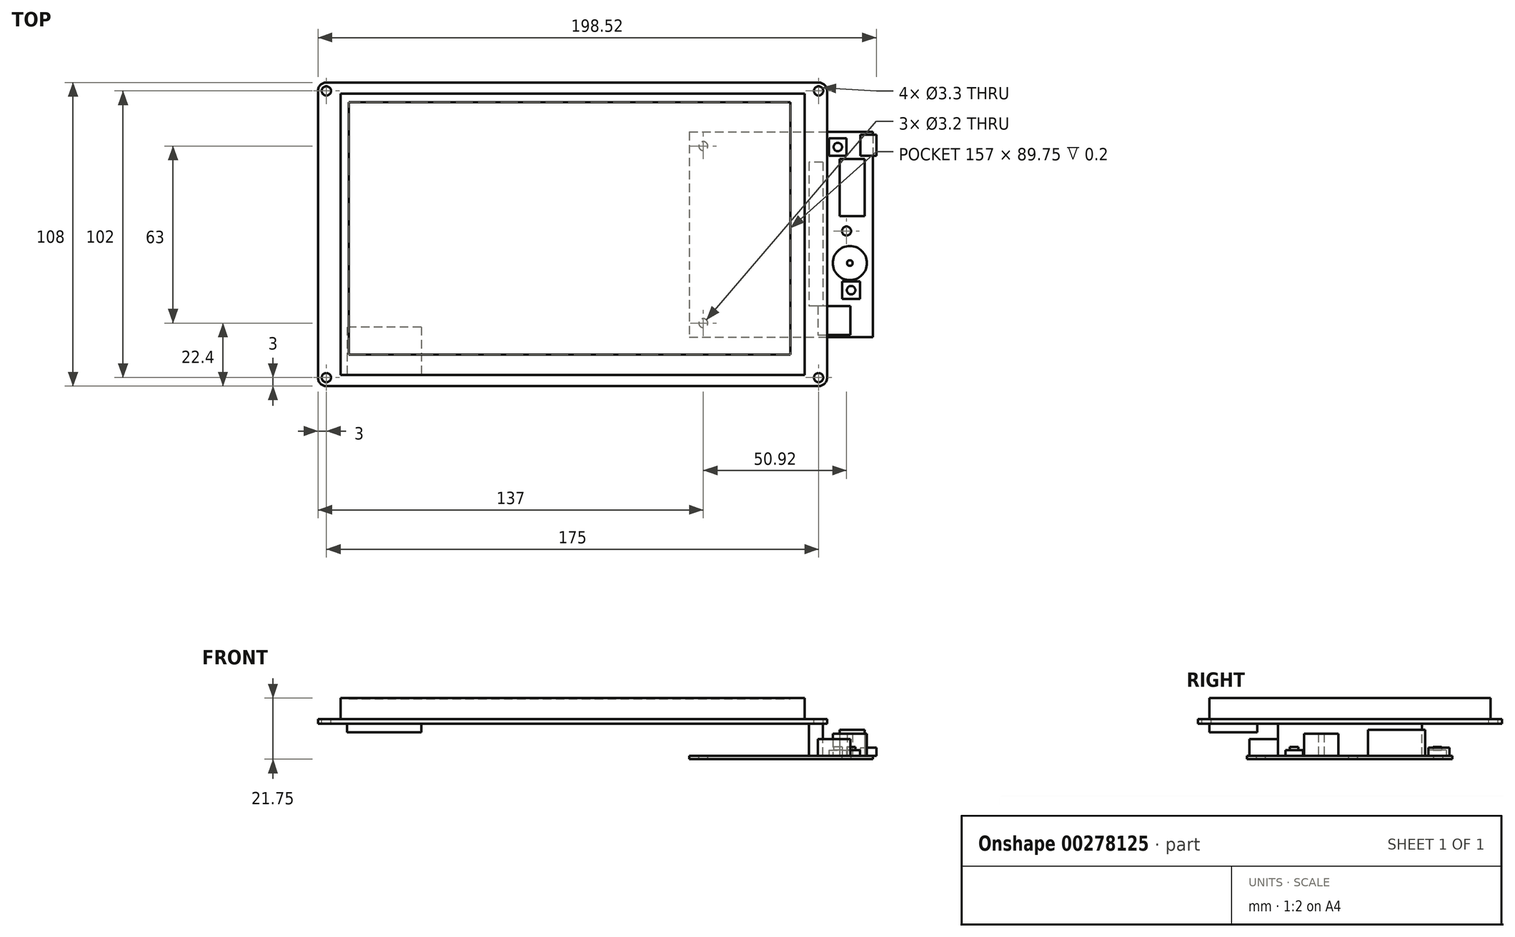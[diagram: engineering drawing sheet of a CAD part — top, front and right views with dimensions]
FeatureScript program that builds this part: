
annotation { "Feature Type Name" : "Feature", "Feature Type Description" : "" }
export const myFeature = defineFeature(function(context is Context, id is Id, definition is map)
    precondition{}
    {
        {
            var Q0;
            Q0=qCreatedBy(makeId("Top.planeOp"),FACE);
            var sketch = newSketch(context, id + "F0", { "sketchPlane" : qUnion([Q0])});
            skLineSegment(sketch, "E0.bottom", {"start": v(87.5, -54) * mm, "end": v(-87.5, -54) * mm});
            skLineSegment(sketch, "E0.top", {"start": v(87.5, 54) * mm, "end": v(-87.5, 54) * mm});
            skLineSegment(sketch, "E0.left", {"start": v(90.5, -51) * mm, "end": v(90.5, 51) * mm});
            skLineSegment(sketch, "E0.right", {"start": v(-90.5, -51) * mm, "end": v(-90.5, 51) * mm});
            skPoint(sketch, "E0.middle", {"position": v(0, 0) * mm});
            skLineSegment(sketch, "E1", {"start": v(0, 54) * mm, "end": v(0, -54) * mm, "construction": true});
            skLineSegment(sketch, "E2", {"start": v(-90.5, 0) * mm, "end": v(90.5, 0) * mm, "construction": true});
            skCircle(sketch, "E3", {"center": v(-87.5, 51) * mm, "radius": 1.65 * mm});
            skCircle(sketch, "E4.MirrorC", {"center": v(87.5, 51) * mm, "radius": 1.65 * mm});
            skCircle(sketch, "E5.MirrorC", {"center": v(-87.5, -51) * mm, "radius": 1.65 * mm});
            skCircle(sketch, "E6.MirrorC", {"center": v(87.5, -51) * mm, "radius": 1.65 * mm});
            skPoint(sketch, "E7.visualSharp", {"position": v(-90.5, 54) * mm});
            skArc(sketch, "E7.filletArc", {"start": v(-87.5, 54) * mm, "mid": v(-89.62, 53.12) * mm, "end": v(-90.5, 51) * mm});
            skPoint(sketch, "E8.visualSharp", {"position": v(-90.5, -54) * mm});
            skArc(sketch, "E8.filletArc", {"start": v(-90.5, -51) * mm, "mid": v(-89.62, -53.12) * mm, "end": v(-87.5, -54) * mm});
            skPoint(sketch, "E9.visualSharp", {"position": v(90.5, -54) * mm});
            skArc(sketch, "E9.filletArc", {"start": v(87.5, -54) * mm, "mid": v(89.62, -53.12) * mm, "end": v(90.5, -51) * mm});
            skPoint(sketch, "E10.visualSharp", {"position": v(90.5, 54) * mm});
            skArc(sketch, "E10.filletArc", {"start": v(90.5, 51) * mm, "mid": v(89.62, 53.12) * mm, "end": v(87.5, 54) * mm});
            skLineSegment(sketch, "E11.bottom", {"start": v(-82.5, 50) * mm, "end": v(82.5, 50) * mm});
            skLineSegment(sketch, "E11.top", {"start": v(-82.5, -50) * mm, "end": v(82.5, -50) * mm});
            skLineSegment(sketch, "E11.left", {"start": v(-82.5, 50) * mm, "end": v(-82.5, -50) * mm});
            skLineSegment(sketch, "E11.right", {"start": v(82.5, 50) * mm, "end": v(82.5, -50) * mm});
            skSolve(sketch);
        }
        {
            var Q0;
            Q0 = qSketchRegion(id + "F0", true);
            var Q1;
            Q1=makeQuery(id+"F0.imprint","IMPRINT",FACE,{"disambiguationData":[TD([[makeQuery(id+"F0.imprint","IMPRINT",EDGE,{"derivedFrom":sQuery(id+"F0.wireOp",EDGE,"E11.bottom")}),-1.0]])]});
            extrude(context, id + "F1", {"entities" : qUnion([Q0, Q1]), "oppositeDirection" : true, "depth" : 1.7 * mm});
        }
        {
            var Q0;
            Q0=makeQuery(id+"F0.imprint","IMPRINT",FACE,{"disambiguationData":[TD([[makeQuery(id+"F0.imprint","IMPRINT",EDGE,{"derivedFrom":sQuery(id+"F0.wireOp",EDGE,"E11.bottom")}),-1.0]])]});
            extrude(context, id + "F2", {"entities" : qUnion([Q0]), "operationType" : NewBodyOperationType.ADD, "depth" : 7.45 * mm});
        }
        {
            var Q0;
            Q0=makeQuery(id+"F2.opExtrude","CAP_FACE",FACE,{"disambiguationData":[OSD([sQuery(id+"F0.wireOp",EDGE,"E11.bottom"),sQuery(id+"F0.wireOp",EDGE,"E11.top"),sQuery(id+"F0.wireOp",EDGE,"E11.left"),sQuery(id+"F0.wireOp",EDGE,"E11.right")])],"isStart":false});
            var sketch = newSketch(context, id + "F3", { "sketchPlane" : qUnion([Q0])});
            skLineSegment(sketch, "E12.bottom", {"start": v(-79.5, 47) * mm, "end": v(77.5, 47) * mm});
            skLineSegment(sketch, "E12.top", {"start": v(-79.5, -42.75) * mm, "end": v(77.5, -42.75) * mm});
            skLineSegment(sketch, "E12.left", {"start": v(-79.5, 47) * mm, "end": v(-79.5, -42.75) * mm});
            skLineSegment(sketch, "E12.right", {"start": v(77.5, 47) * mm, "end": v(77.5, -42.75) * mm});
            skSolve(sketch);
        }
        {
            var Q0;
            Q0=makeQuery(id+"F3.imprint","IMPRINT",FACE,{"disambiguationData":[TD([[makeQuery(id+"F3.imprint","IMPRINT",EDGE,{"derivedFrom":sQuery(id+"F3.wireOp",EDGE,"E12.bottom")}),-1.0]])]});
            extrude(context, id + "F4", {"entities" : qUnion([Q0]), "operationType" : NewBodyOperationType.REMOVE, "oppositeDirection" : true, "depth" : 0.2 * mm});
        }
        {
            var Q0;
            Q0=makeQuery(id+"F1.opExtrude","CAP_FACE",FACE,{"disambiguationData":[OSD([sQuery(id+"F0.wireOp",EDGE,"E0.bottom"),sQuery(id+"F0.wireOp",EDGE,"E0.top"),sQuery(id+"F0.wireOp",EDGE,"E0.left"),sQuery(id+"F0.wireOp",EDGE,"E0.right"),sQuery(id+"F0.wireOp",EDGE,"E3"),sQuery(id+"F0.wireOp",EDGE,"E4.MirrorC"),sQuery(id+"F0.wireOp",EDGE,"E5.MirrorC"),sQuery(id+"F0.wireOp",EDGE,"E6.MirrorC"),sQuery(id+"F0.wireOp",EDGE,"E7.filletArc"),sQuery(id+"F0.wireOp",EDGE,"E8.filletArc"),sQuery(id+"F0.wireOp",EDGE,"E9.filletArc"),sQuery(id+"F0.wireOp",EDGE,"E10.filletArc")])],"isStart":false});
            var sketch = newSketch(context, id + "F5", { "sketchPlane" : qUnion([Q0])});
            skLineSegment(sketch, "E13.bottom", {"start": v(89, -25.6) * mm, "end": v(84, -25.6) * mm});
            skLineSegment(sketch, "E13.top", {"start": v(89, 25.56) * mm, "end": v(84, 25.56) * mm});
            skLineSegment(sketch, "E13.left", {"start": v(89, -25.6) * mm, "end": v(89, 25.56) * mm});
            skLineSegment(sketch, "E13.right", {"start": v(84, -25.6) * mm, "end": v(84, 25.56) * mm});
            skLineSegment(sketch, "E14.bottom", {"start": v(-53.8, 33) * mm, "end": v(-80.2, 33) * mm});
            skLineSegment(sketch, "E14.top", {"start": v(-53.8, 50) * mm, "end": v(-80.2, 50) * mm});
            skLineSegment(sketch, "E14.left", {"start": v(-53.8, 33) * mm, "end": v(-53.8, 50) * mm});
            skLineSegment(sketch, "E14.right", {"start": v(-80.2, 33) * mm, "end": v(-80.2, 50) * mm});
            skSolve(sketch);
        }
        {
            var Q0;
            Q0=makeQuery(id+"F5.imprint","IMPRINT",FACE,{"disambiguationData":[TD([[makeQuery(id+"F5.imprint","IMPRINT",EDGE,{"derivedFrom":sQuery(id+"F5.wireOp",EDGE,"E13.bottom")}),-1.0]])]});
            extrude(context, id + "F6", {"entities" : qUnion([Q0]), "operationType" : NewBodyOperationType.ADD, "depth" : 11.4 * mm});
        }
        {
            var Q0;
            Q0=makeQuery(id+"F5.imprint","IMPRINT",FACE,{"disambiguationData":[TD([[makeQuery(id+"F5.imprint","IMPRINT",EDGE,{"derivedFrom":sQuery(id+"F5.wireOp",EDGE,"E14.bottom")}),-1.0]])]});
            extrude(context, id + "F7", {"entities" : qUnion([Q0]), "operationType" : NewBodyOperationType.ADD, "depth" : 3 * mm});
        }
        {
            var Q0;
            Q0=makeQuery(id+"F6.opExtrude","CAP_FACE",FACE,{"disambiguationData":[OSD([sQuery(id+"F5.wireOp",EDGE,"E13.bottom"),sQuery(id+"F5.wireOp",EDGE,"E13.top"),sQuery(id+"F5.wireOp",EDGE,"E13.left"),sQuery(id+"F5.wireOp",EDGE,"E13.right")])],"isStart":false});
            var sketch = newSketch(context, id + "F8", { "sketchPlane" : qUnion([Q0])});
            skLineSegment(sketch, "E15.0", {"start": v(84, -25.6) * mm, "end": v(84, 25.56) * mm, "construction": true});
            skLineSegment(sketch, "E15.1", {"start": v(89, -25.6) * mm, "end": v(89, 25.56) * mm, "construction": true});
            skLineSegment(sketch, "E15.2", {"start": v(89, -25.6) * mm, "end": v(84, -25.6) * mm, "construction": true});
            skLineSegment(sketch, "E15.3", {"start": v(89, 25.56) * mm, "end": v(84, 25.56) * mm, "construction": true});
            skLineSegment(sketch, "E16.bottom", {"start": v(41.5, -36.4) * mm, "end": v(106.82, -36.4) * mm});
            skLineSegment(sketch, "E16.top", {"start": v(41.5, 36.6) * mm, "end": v(106.82, 36.6) * mm});
            skLineSegment(sketch, "E16.left", {"start": v(41.5, -36.4) * mm, "end": v(41.5, 36.6) * mm});
            skLineSegment(sketch, "E16.right", {"start": v(106.82, -36.4) * mm, "end": v(106.82, 36.6) * mm});
            skCircle(sketch, "E17", {"center": v(46.5, -31.4) * mm, "radius": 1.6 * mm});
            skLineSegment(sketch, "E18", {"start": v(41.5, 0.1) * mm, "end": v(106.82, 0.1) * mm, "construction": true});
            skCircle(sketch, "E19.MirrorC", {"center": v(46.5, 31.6) * mm, "radius": 1.6 * mm});
            skCircle(sketch, "E20", {"center": v(97.42, -1.15) * mm, "radius": 1.6 * mm});
            skSolve(sketch);
        }
        {
            var Q0;
            Q0=makeQuery(id+"F8.imprint","IMPRINT",FACE,{"disambiguationData":[TD([[makeQuery(id+"F8.imprint","IMPRINT",EDGE,{"derivedFrom":sQuery(id+"F8.wireOp",EDGE,"E16.bottom")}),1.0]])]});
            var Q1;
            Q1=makeQuery(id+"F8.imprint","IMPRINT",FACE,{"disambiguationData":[TD([[makeQuery(id+"F8.imprint","IMPRINT",EDGE,{"derivedFrom":makeQuery(id+"F6.opExtrude","CAP_EDGE",EDGE,{"disambiguationData":[OSD([sQuery(id+"F5.wireOp",EDGE,"E13.bottom")])],"isStart":false})}),-1.0]])]});
            extrude(context, id + "F9", {"entities" : qUnion([Q0, Q1]), "operationType" : NewBodyOperationType.ADD, "depth" : 1.2 * mm});
        }
        {
            var Q0;
            Q0=makeQuery(id+"F9.opExtrude","CAP_FACE",FACE,{"disambiguationData":[OSD([sQuery(id+"F8.wireOp",EDGE,"E16.bottom"),sQuery(id+"F8.wireOp",EDGE,"E16.top"),sQuery(id+"F8.wireOp",EDGE,"E16.left"),sQuery(id+"F8.wireOp",EDGE,"E16.right"),sQuery(id+"F8.wireOp",EDGE,"E17"),sQuery(id+"F8.wireOp",EDGE,"E19.MirrorC"),sQuery(id+"F8.wireOp",EDGE,"E20")])],"isStart":true});
            var sketch = newSketch(context, id + "F10", { "sketchPlane" : qUnion([Q0])});
            skLineSegment(sketch, "E21.0", {"start": v(106.82, 36.4) * mm, "end": v(106.82, -36.6) * mm, "construction": true});
            skLineSegment(sketch, "E21.1", {"start": v(41.5, 36.4) * mm, "end": v(106.82, 36.4) * mm, "construction": true});
            skLineSegment(sketch, "E21.2", {"start": v(41.5, -36.6) * mm, "end": v(106.82, -36.6) * mm, "construction": true});
            skLineSegment(sketch, "E21.3", {"start": v(41.5, 36.4) * mm, "end": v(41.5, -36.6) * mm, "construction": true});
            skLineSegment(sketch, "E22.bottom", {"start": v(87.19, -25.56) * mm, "end": v(98.82, -25.56) * mm});
            skLineSegment(sketch, "E22.top", {"start": v(87.19, -35.79) * mm, "end": v(98.82, -35.79) * mm});
            skLineSegment(sketch, "E22.left", {"start": v(87.19, -25.56) * mm, "end": v(87.19, -35.79) * mm});
            skLineSegment(sketch, "E22.right", {"start": v(98.82, -25.56) * mm, "end": v(98.82, -35.79) * mm});
            skLineSegment(sketch, "E23.bottom", {"start": v(95.92, -16.75) * mm, "end": v(102.17, -16.75) * mm});
            skLineSegment(sketch, "E23.top", {"start": v(95.92, -23) * mm, "end": v(102.17, -23) * mm});
            skLineSegment(sketch, "E23.left", {"start": v(95.92, -16.75) * mm, "end": v(95.92, -23) * mm});
            skLineSegment(sketch, "E23.right", {"start": v(102.17, -16.75) * mm, "end": v(102.17, -23) * mm});
            skLineSegment(sketch, "E24.bottom", {"start": v(103.92, 6.45) * mm, "end": v(94.92, 6.45) * mm});
            skLineSegment(sketch, "E24.top", {"start": v(103.92, 26.75) * mm, "end": v(94.92, 26.75) * mm});
            skLineSegment(sketch, "E24.left", {"start": v(103.92, 6.45) * mm, "end": v(103.92, 26.75) * mm});
            skLineSegment(sketch, "E24.right", {"start": v(94.92, 6.45) * mm, "end": v(94.92, 26.75) * mm});
            skLineSegment(sketch, "E25.bottom", {"start": v(102.32, 35.4) * mm, "end": v(108.02, 35.4) * mm});
            skLineSegment(sketch, "E25.top", {"start": v(102.32, 27.9) * mm, "end": v(108.02, 27.9) * mm});
            skLineSegment(sketch, "E25.left", {"start": v(102.32, 35.4) * mm, "end": v(102.32, 27.9) * mm});
            skLineSegment(sketch, "E25.right", {"start": v(108.02, 35.4) * mm, "end": v(108.02, 27.9) * mm});
            skLineSegment(sketch, "E26.bottom", {"start": v(91.2, 34.15) * mm, "end": v(97.45, 34.15) * mm});
            skLineSegment(sketch, "E26.top", {"start": v(91.2, 27.9) * mm, "end": v(97.45, 27.9) * mm});
            skLineSegment(sketch, "E26.left", {"start": v(91.2, 34.15) * mm, "end": v(91.2, 27.9) * mm});
            skLineSegment(sketch, "E26.right", {"start": v(97.45, 34.15) * mm, "end": v(97.45, 27.9) * mm});
            skCircle(sketch, "E27", {"center": v(98.6, -10.24) * mm, "radius": 6.08 * mm});
            skCircle(sketch, "E28", {"center": v(99.04, -19.87) * mm, "radius": 1.5 * mm});
            skPoint(sketch, "E28.centerSnap0", {"position": v(95.92, -19.87) * mm});
            skPoint(sketch, "E28.centerSnap1", {"position": v(99.04, -16.75) * mm});
            skCircle(sketch, "E29", {"center": v(94.32, 31.03) * mm, "radius": 1.5 * mm});
            skPoint(sketch, "E29.centerSnap0", {"position": v(91.2, 31.03) * mm});
            skPoint(sketch, "E29.centerSnap1", {"position": v(94.32, 34.15) * mm});
            skCircle(sketch, "E30", {"center": v(98.6, -10.24) * mm, "radius": 1 * mm});
            skSolve(sketch);
        }
        {
            var Q0;
            Q0=makeQuery(id+"F10.imprint","IMPRINT",FACE,{"disambiguationData":[TD([[makeQuery(id+"F10.imprint","IMPRINT",EDGE,{"derivedFrom":sQuery(id+"F10.wireOp",EDGE,"E22.top")}),1.0]])]});
            extrude(context, id + "F11", {"entities" : qUnion([Q0]), "operationType" : NewBodyOperationType.ADD, "depth" : 6 * mm});
        }
        {
            var Q0;
            Q0=makeQuery(id+"F10.imprint","IMPRINT",FACE,{"disambiguationData":[TD([[makeQuery(id+"F10.imprint","IMPRINT",EDGE,{"derivedFrom":sQuery(id+"F10.wireOp",EDGE,"E27")}),1.0]])]});
            extrude(context, id + "F12", {"entities" : qUnion([Q0]), "operationType" : NewBodyOperationType.ADD, "depth" : 7.85 * mm});
        }
        {
            var Q0;
            Q0=makeQuery(id+"F10.imprint","IMPRINT",FACE,{"disambiguationData":[TD([[makeQuery(id+"F10.imprint","IMPRINT",EDGE,{"derivedFrom":sQuery(id+"F10.wireOp",EDGE,"E24.bottom")}),-1.0]])]});
            extrude(context, id + "F13", {"entities" : qUnion([Q0]), "operationType" : NewBodyOperationType.ADD, "depth" : 9.25 * mm});
        }
        {
            var Q0;
            Q0=makeQuery(id+"F10.imprint","IMPRINT",FACE,{"disambiguationData":[TD([[makeQuery(id+"F10.imprint","IMPRINT",EDGE,{"derivedFrom":sQuery(id+"F10.wireOp",EDGE,"E29")}),1.0]])]});
            var Q1;
            Q1=makeQuery(id+"F10.imprint","IMPRINT",FACE,{"disambiguationData":[TD([[makeQuery(id+"F10.imprint","IMPRINT",EDGE,{"derivedFrom":sQuery(id+"F10.wireOp",EDGE,"E28")}),1.0]])]});
            extrude(context, id + "F14", {"entities" : qUnion([Q0, Q1]), "operationType" : NewBodyOperationType.ADD, "depth" : (4.35 - 1.2) * mm});
        }
        {
            var Q0;
            Q0=makeQuery(id+"F10.imprint","IMPRINT",FACE,{"disambiguationData":[TD([[makeQuery(id+"F10.imprint","IMPRINT",EDGE,{"derivedFrom":sQuery(id+"F10.wireOp",EDGE,"E26.bottom")}),-1.0]])]});
            var Q1;
            Q1=makeQuery(id+"F10.imprint","IMPRINT",FACE,{"disambiguationData":[TD([[makeQuery(id+"F10.imprint","IMPRINT",EDGE,{"derivedFrom":sQuery(id+"F10.wireOp",EDGE,"E23.bottom")}),-1.0]])]});
            extrude(context, id + "F15", {"entities" : qUnion([Q0, Q1]), "operationType" : NewBodyOperationType.ADD, "depth" : 2 * mm});
        }
        {
            var Q0;
            {var subQ0=sQuery(id+"F10.wireOp",EDGE,"E25.right");Q0=makeQuery(id+"F10.imprint","IMPRINT",FACE,{"disambiguationData":[TD([[makeQuery(id+"F10.imprint","IMPRINT",EDGE,{"derivedFrom":subQ0}),-1.0]])]});}
            var Q1;
            {var subQ0=sQuery(id+"F10.wireOp",EDGE,"E25.left");Q1=makeQuery(id+"F10.imprint","IMPRINT",FACE,{"disambiguationData":[TD([[makeQuery(id+"F10.imprint","IMPRINT",EDGE,{"derivedFrom":subQ0}),1.0]])]});}
            extrude(context, id + "F16", {"entities" : qUnion([Q0, Q1]), "operationType" : NewBodyOperationType.ADD, "depth" : 2.9 * mm});
        }
    });
